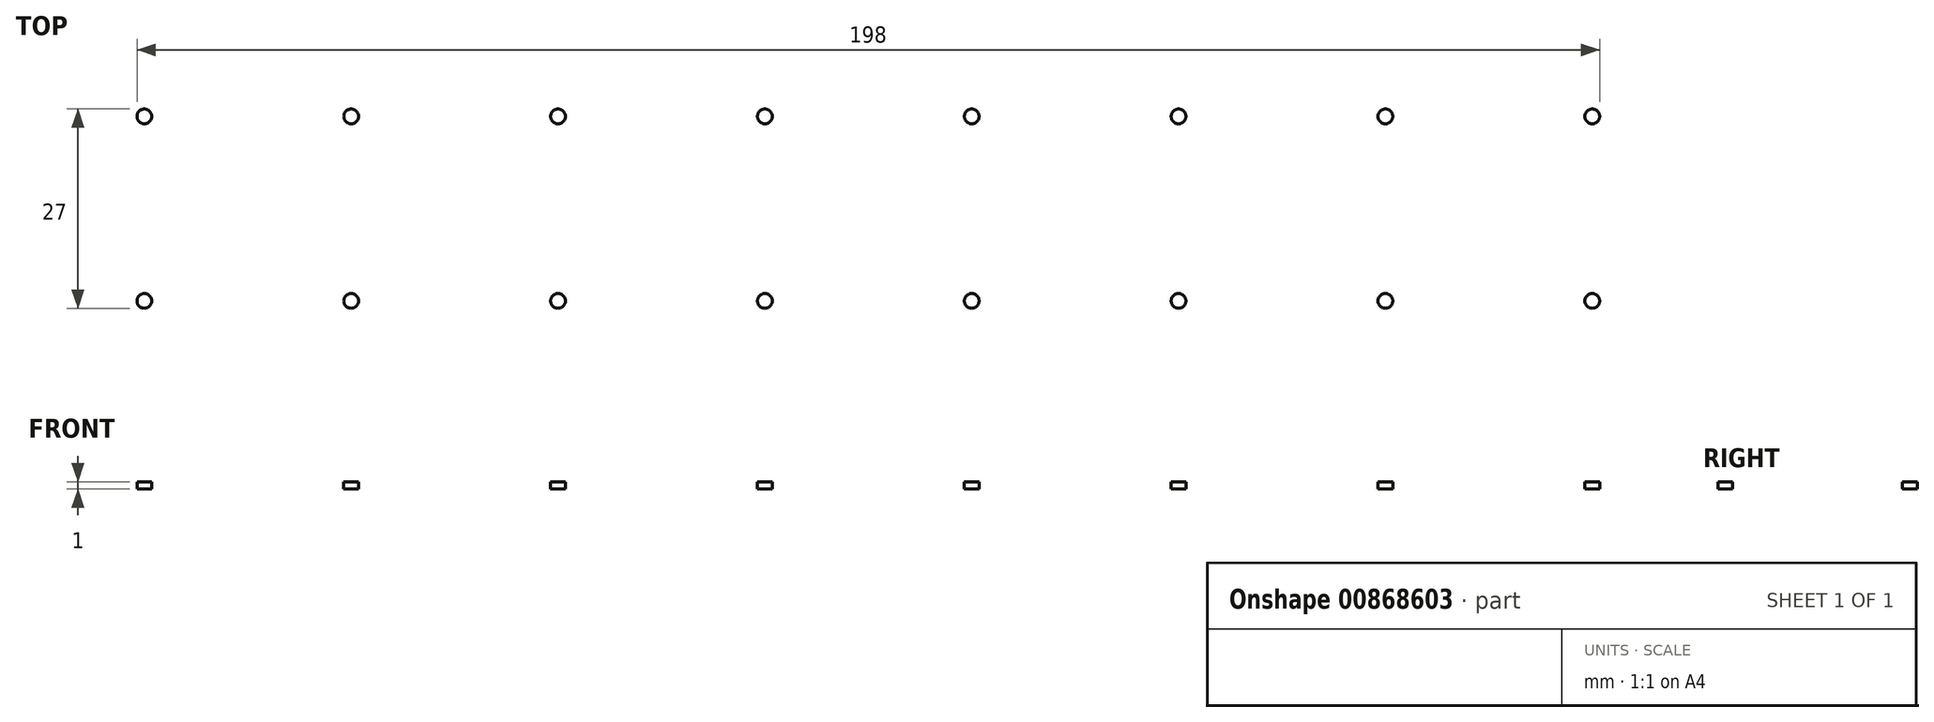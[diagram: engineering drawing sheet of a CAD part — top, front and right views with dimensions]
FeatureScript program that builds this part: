
annotation { "Feature Type Name" : "Feature", "Feature Type Description" : "" }
export const myFeature = defineFeature(function(context is Context, id is Id, definition is map)
    precondition{}
    {
        {
            var Q0;
            Q0=qCreatedBy(makeId("Top.planeOp"),FACE);
            var sketch = newSketch(context, id + "F0", { "sketchPlane" : qUnion([Q0])});
            skCircle(sketch, "E0", {"center": v(0, 0) * mm, "radius": 1 * mm});
            skLineSegment(sketch, "E1", {"start": v(-1, 0) * mm, "end": v(1, 0) * mm});
            skLineSegment(sketch, "E2", {"start": v(1, 0) * mm, "end": v(0, 0) * mm});
            skLineSegment(sketch, "E3", {"start": v(0, -1) * mm, "end": v(0, 1) * mm});
            skCircle(sketch, "E4.0.1.0", {"center": v(0, 25) * mm, "radius": 1 * mm});
            skLineSegment(sketch, "E4.0.1.1", {"start": v(-1, 25) * mm, "end": v(1, 25) * mm});
            skLineSegment(sketch, "E4.0.1.2", {"start": v(1, 25) * mm, "end": v(0, 25) * mm});
            skLineSegment(sketch, "E4.0.1.3", {"start": v(0, 24) * mm, "end": v(0, 26) * mm});
            skCircle(sketch, "E4.1.0.0", {"center": v(28, 0) * mm, "radius": 1 * mm});
            skLineSegment(sketch, "E4.1.0.1", {"start": v(27, 0) * mm, "end": v(29, 0) * mm});
            skLineSegment(sketch, "E4.1.0.2", {"start": v(29, 0) * mm, "end": v(28, 0) * mm});
            skLineSegment(sketch, "E4.1.0.3", {"start": v(28, -1) * mm, "end": v(28, 1) * mm});
            skCircle(sketch, "E4.1.1.0", {"center": v(28, 25) * mm, "radius": 1 * mm});
            skLineSegment(sketch, "E4.1.1.1", {"start": v(27, 25) * mm, "end": v(29, 25) * mm});
            skLineSegment(sketch, "E4.1.1.2", {"start": v(29, 25) * mm, "end": v(28, 25) * mm});
            skLineSegment(sketch, "E4.1.1.3", {"start": v(28, 24) * mm, "end": v(28, 26) * mm});
            skCircle(sketch, "E4.2.0.0", {"center": v(56, 0) * mm, "radius": 1 * mm});
            skLineSegment(sketch, "E4.2.0.1", {"start": v(55, 0) * mm, "end": v(57, 0) * mm});
            skLineSegment(sketch, "E4.2.0.2", {"start": v(57, 0) * mm, "end": v(56, 0) * mm});
            skLineSegment(sketch, "E4.2.0.3", {"start": v(56, -1) * mm, "end": v(56, 1) * mm});
            skCircle(sketch, "E4.2.1.0", {"center": v(56, 25) * mm, "radius": 1 * mm});
            skLineSegment(sketch, "E4.2.1.1", {"start": v(55, 25) * mm, "end": v(57, 25) * mm});
            skLineSegment(sketch, "E4.2.1.2", {"start": v(57, 25) * mm, "end": v(56, 25) * mm});
            skLineSegment(sketch, "E4.2.1.3", {"start": v(56, 24) * mm, "end": v(56, 26) * mm});
            skCircle(sketch, "E4.3.0.0", {"center": v(84, 0) * mm, "radius": 1 * mm});
            skLineSegment(sketch, "E4.3.0.1", {"start": v(83, 0) * mm, "end": v(85, 0) * mm});
            skLineSegment(sketch, "E4.3.0.2", {"start": v(85, 0) * mm, "end": v(84, 0) * mm});
            skLineSegment(sketch, "E4.3.0.3", {"start": v(84, -1) * mm, "end": v(84, 1) * mm});
            skCircle(sketch, "E4.3.1.0", {"center": v(84, 25) * mm, "radius": 1 * mm});
            skLineSegment(sketch, "E4.3.1.1", {"start": v(83, 25) * mm, "end": v(85, 25) * mm});
            skLineSegment(sketch, "E4.3.1.2", {"start": v(85, 25) * mm, "end": v(84, 25) * mm});
            skLineSegment(sketch, "E4.3.1.3", {"start": v(84, 24) * mm, "end": v(84, 26) * mm});
            skCircle(sketch, "E4.4.0.0", {"center": v(112, 0) * mm, "radius": 1 * mm});
            skLineSegment(sketch, "E4.4.0.1", {"start": v(111, 0) * mm, "end": v(113, 0) * mm});
            skLineSegment(sketch, "E4.4.0.2", {"start": v(113, 0) * mm, "end": v(112, 0) * mm});
            skLineSegment(sketch, "E4.4.0.3", {"start": v(112, -1) * mm, "end": v(112, 1) * mm});
            skCircle(sketch, "E4.4.1.0", {"center": v(112, 25) * mm, "radius": 1 * mm});
            skLineSegment(sketch, "E4.4.1.1", {"start": v(111, 25) * mm, "end": v(113, 25) * mm});
            skLineSegment(sketch, "E4.4.1.2", {"start": v(113, 25) * mm, "end": v(112, 25) * mm});
            skLineSegment(sketch, "E4.4.1.3", {"start": v(112, 24) * mm, "end": v(112, 26) * mm});
            skCircle(sketch, "E4.5.0.0", {"center": v(140, 0) * mm, "radius": 1 * mm});
            skLineSegment(sketch, "E4.5.0.1", {"start": v(139, 0) * mm, "end": v(141, 0) * mm});
            skLineSegment(sketch, "E4.5.0.2", {"start": v(141, 0) * mm, "end": v(140, 0) * mm});
            skLineSegment(sketch, "E4.5.0.3", {"start": v(140, -1) * mm, "end": v(140, 1) * mm});
            skCircle(sketch, "E4.5.1.0", {"center": v(140, 25) * mm, "radius": 1 * mm});
            skLineSegment(sketch, "E4.5.1.1", {"start": v(139, 25) * mm, "end": v(141, 25) * mm});
            skLineSegment(sketch, "E4.5.1.2", {"start": v(141, 25) * mm, "end": v(140, 25) * mm});
            skLineSegment(sketch, "E4.5.1.3", {"start": v(140, 24) * mm, "end": v(140, 26) * mm});
            skCircle(sketch, "E4.6.0.0", {"center": v(168, 0) * mm, "radius": 1 * mm});
            skLineSegment(sketch, "E4.6.0.1", {"start": v(167, 0) * mm, "end": v(169, 0) * mm});
            skLineSegment(sketch, "E4.6.0.2", {"start": v(169, 0) * mm, "end": v(168, 0) * mm});
            skLineSegment(sketch, "E4.6.0.3", {"start": v(168, -1) * mm, "end": v(168, 1) * mm});
            skCircle(sketch, "E4.6.1.0", {"center": v(168, 25) * mm, "radius": 1 * mm});
            skLineSegment(sketch, "E4.6.1.1", {"start": v(167, 25) * mm, "end": v(169, 25) * mm});
            skLineSegment(sketch, "E4.6.1.2", {"start": v(169, 25) * mm, "end": v(168, 25) * mm});
            skLineSegment(sketch, "E4.6.1.3", {"start": v(168, 24) * mm, "end": v(168, 26) * mm});
            skCircle(sketch, "E4.7.0.0", {"center": v(196, 0) * mm, "radius": 1 * mm});
            skLineSegment(sketch, "E4.7.0.1", {"start": v(195, 0) * mm, "end": v(197, 0) * mm});
            skLineSegment(sketch, "E4.7.0.2", {"start": v(197, 0) * mm, "end": v(196, 0) * mm});
            skLineSegment(sketch, "E4.7.0.3", {"start": v(196, -1) * mm, "end": v(196, 1) * mm});
            skCircle(sketch, "E4.7.1.0", {"center": v(196, 25) * mm, "radius": 1 * mm});
            skLineSegment(sketch, "E4.7.1.1", {"start": v(195, 25) * mm, "end": v(197, 25) * mm});
            skLineSegment(sketch, "E4.7.1.2", {"start": v(197, 25) * mm, "end": v(196, 25) * mm});
            skLineSegment(sketch, "E4.7.1.3", {"start": v(196, 24) * mm, "end": v(196, 26) * mm});
            skLineSegment(sketch, "E4.direction1", {"start": v(0, -1) * mm, "end": v(28, -1) * mm, "construction": true});
            skLineSegment(sketch, "E4.direction2", {"start": v(0, -1) * mm, "end": v(0, 24) * mm, "construction": true});
            skSolve(sketch);
        }
        {
            var Q0;
            {var subQ0=sQuery(id+"F0.wireOp",EDGE,"E4.7.1.2");Q0=makeQuery(id+"F0.imprint","IMPRINT",FACE,{"disambiguationData":[TD([[makeQuery(id+"F0.imprint","IMPRINT",EDGE,{"derivedFrom":subQ0}),1.0]])]});}
            var Q1;
            {var subQ0=sQuery(id+"F0.wireOp",EDGE,"E4.7.1.1");Q1=makeQuery(id+"F0.imprint","IMPRINT",FACE,{"disambiguationData":[TD([[makeQuery(id+"F0.imprint","IMPRINT",EDGE,{"derivedFrom":subQ0}),1.0]])]});}
            var Q2;
            {var subQ0=sQuery(id+"F0.wireOp",EDGE,"E4.7.1.1");Q2=makeQuery(id+"F0.imprint","IMPRINT",FACE,{"disambiguationData":[TD([[makeQuery(id+"F0.imprint","IMPRINT",EDGE,{"derivedFrom":subQ0}),-1.0]])]});}
            var Q3;
            {var subQ0=sQuery(id+"F0.wireOp",EDGE,"E4.7.1.2");Q3=makeQuery(id+"F0.imprint","IMPRINT",FACE,{"disambiguationData":[TD([[makeQuery(id+"F0.imprint","IMPRINT",EDGE,{"derivedFrom":subQ0}),-1.0]])]});}
            var Q4;
            {var subQ0=sQuery(id+"F0.wireOp",EDGE,"E4.6.1.2");Q4=makeQuery(id+"F0.imprint","IMPRINT",FACE,{"disambiguationData":[TD([[makeQuery(id+"F0.imprint","IMPRINT",EDGE,{"derivedFrom":subQ0}),-1.0]])]});}
            var Q5;
            {var subQ0=sQuery(id+"F0.wireOp",EDGE,"E4.6.1.1");Q5=makeQuery(id+"F0.imprint","IMPRINT",FACE,{"disambiguationData":[TD([[makeQuery(id+"F0.imprint","IMPRINT",EDGE,{"derivedFrom":subQ0}),1.0]])]});}
            var Q6;
            {var subQ0=sQuery(id+"F0.wireOp",EDGE,"E4.6.1.1");Q6=makeQuery(id+"F0.imprint","IMPRINT",FACE,{"disambiguationData":[TD([[makeQuery(id+"F0.imprint","IMPRINT",EDGE,{"derivedFrom":subQ0}),-1.0]])]});}
            var Q7;
            {var subQ0=sQuery(id+"F0.wireOp",EDGE,"E4.6.1.2");Q7=makeQuery(id+"F0.imprint","IMPRINT",FACE,{"disambiguationData":[TD([[makeQuery(id+"F0.imprint","IMPRINT",EDGE,{"derivedFrom":subQ0}),1.0]])]});}
            var Q8;
            {var subQ0=sQuery(id+"F0.wireOp",EDGE,"E4.7.0.2");Q8=makeQuery(id+"F0.imprint","IMPRINT",FACE,{"disambiguationData":[TD([[makeQuery(id+"F0.imprint","IMPRINT",EDGE,{"derivedFrom":subQ0}),-1.0]])]});}
            var Q9;
            {var subQ0=sQuery(id+"F0.wireOp",EDGE,"E4.7.0.1");Q9=makeQuery(id+"F0.imprint","IMPRINT",FACE,{"disambiguationData":[TD([[makeQuery(id+"F0.imprint","IMPRINT",EDGE,{"derivedFrom":subQ0}),1.0]])]});}
            var Q10;
            {var subQ0=sQuery(id+"F0.wireOp",EDGE,"E4.7.0.1");Q10=makeQuery(id+"F0.imprint","IMPRINT",FACE,{"disambiguationData":[TD([[makeQuery(id+"F0.imprint","IMPRINT",EDGE,{"derivedFrom":subQ0}),-1.0]])]});}
            var Q11;
            {var subQ0=sQuery(id+"F0.wireOp",EDGE,"E4.7.0.2");Q11=makeQuery(id+"F0.imprint","IMPRINT",FACE,{"disambiguationData":[TD([[makeQuery(id+"F0.imprint","IMPRINT",EDGE,{"derivedFrom":subQ0}),1.0]])]});}
            var Q12;
            {var subQ0=sQuery(id+"F0.wireOp",EDGE,"E4.0.1.2");Q12=makeQuery(id+"F0.imprint","IMPRINT",FACE,{"disambiguationData":[TD([[makeQuery(id+"F0.imprint","IMPRINT",EDGE,{"derivedFrom":subQ0}),-1.0]])]});}
            var Q13;
            {var subQ0=sQuery(id+"F0.wireOp",EDGE,"E4.0.1.1");Q13=makeQuery(id+"F0.imprint","IMPRINT",FACE,{"disambiguationData":[TD([[makeQuery(id+"F0.imprint","IMPRINT",EDGE,{"derivedFrom":subQ0}),1.0]])]});}
            var Q14;
            {var subQ0=sQuery(id+"F0.wireOp",EDGE,"E4.0.1.1");Q14=makeQuery(id+"F0.imprint","IMPRINT",FACE,{"disambiguationData":[TD([[makeQuery(id+"F0.imprint","IMPRINT",EDGE,{"derivedFrom":subQ0}),-1.0]])]});}
            var Q15;
            {var subQ0=sQuery(id+"F0.wireOp",EDGE,"E4.0.1.2");Q15=makeQuery(id+"F0.imprint","IMPRINT",FACE,{"disambiguationData":[TD([[makeQuery(id+"F0.imprint","IMPRINT",EDGE,{"derivedFrom":subQ0}),1.0]])]});}
            var Q16;
            {var subQ0=sQuery(id+"F0.wireOp",EDGE,"E4.1.0.2");Q16=makeQuery(id+"F0.imprint","IMPRINT",FACE,{"disambiguationData":[TD([[makeQuery(id+"F0.imprint","IMPRINT",EDGE,{"derivedFrom":subQ0}),-1.0]])]});}
            var Q17;
            {var subQ0=sQuery(id+"F0.wireOp",EDGE,"E4.1.0.1");Q17=makeQuery(id+"F0.imprint","IMPRINT",FACE,{"disambiguationData":[TD([[makeQuery(id+"F0.imprint","IMPRINT",EDGE,{"derivedFrom":subQ0}),1.0]])]});}
            var Q18;
            {var subQ0=sQuery(id+"F0.wireOp",EDGE,"E4.1.0.1");Q18=makeQuery(id+"F0.imprint","IMPRINT",FACE,{"disambiguationData":[TD([[makeQuery(id+"F0.imprint","IMPRINT",EDGE,{"derivedFrom":subQ0}),-1.0]])]});}
            var Q19;
            {var subQ0=sQuery(id+"F0.wireOp",EDGE,"E4.1.0.2");Q19=makeQuery(id+"F0.imprint","IMPRINT",FACE,{"disambiguationData":[TD([[makeQuery(id+"F0.imprint","IMPRINT",EDGE,{"derivedFrom":subQ0}),1.0]])]});}
            var Q20;
            {var subQ0=sQuery(id+"F0.wireOp",EDGE,"E4.1.1.2");Q20=makeQuery(id+"F0.imprint","IMPRINT",FACE,{"disambiguationData":[TD([[makeQuery(id+"F0.imprint","IMPRINT",EDGE,{"derivedFrom":subQ0}),1.0]])]});}
            var Q21;
            {var subQ0=sQuery(id+"F0.wireOp",EDGE,"E4.1.1.1");Q21=makeQuery(id+"F0.imprint","IMPRINT",FACE,{"disambiguationData":[TD([[makeQuery(id+"F0.imprint","IMPRINT",EDGE,{"derivedFrom":subQ0}),1.0]])]});}
            var Q22;
            {var subQ0=sQuery(id+"F0.wireOp",EDGE,"E4.1.1.1");Q22=makeQuery(id+"F0.imprint","IMPRINT",FACE,{"disambiguationData":[TD([[makeQuery(id+"F0.imprint","IMPRINT",EDGE,{"derivedFrom":subQ0}),-1.0]])]});}
            var Q23;
            {var subQ0=sQuery(id+"F0.wireOp",EDGE,"E4.2.0.2");Q23=makeQuery(id+"F0.imprint","IMPRINT",FACE,{"disambiguationData":[TD([[makeQuery(id+"F0.imprint","IMPRINT",EDGE,{"derivedFrom":subQ0}),-1.0]])]});}
            var Q24;
            {var subQ0=sQuery(id+"F0.wireOp",EDGE,"E4.2.0.1");Q24=makeQuery(id+"F0.imprint","IMPRINT",FACE,{"disambiguationData":[TD([[makeQuery(id+"F0.imprint","IMPRINT",EDGE,{"derivedFrom":subQ0}),1.0]])]});}
            var Q25;
            {var subQ0=sQuery(id+"F0.wireOp",EDGE,"E4.2.0.1");Q25=makeQuery(id+"F0.imprint","IMPRINT",FACE,{"disambiguationData":[TD([[makeQuery(id+"F0.imprint","IMPRINT",EDGE,{"derivedFrom":subQ0}),-1.0]])]});}
            var Q26;
            {var subQ0=sQuery(id+"F0.wireOp",EDGE,"E4.2.0.2");Q26=makeQuery(id+"F0.imprint","IMPRINT",FACE,{"disambiguationData":[TD([[makeQuery(id+"F0.imprint","IMPRINT",EDGE,{"derivedFrom":subQ0}),1.0]])]});}
            var Q27;
            {var subQ0=sQuery(id+"F0.wireOp",EDGE,"E4.2.1.2");Q27=makeQuery(id+"F0.imprint","IMPRINT",FACE,{"disambiguationData":[TD([[makeQuery(id+"F0.imprint","IMPRINT",EDGE,{"derivedFrom":subQ0}),-1.0]])]});}
            var Q28;
            {var subQ0=sQuery(id+"F0.wireOp",EDGE,"E4.2.1.1");Q28=makeQuery(id+"F0.imprint","IMPRINT",FACE,{"disambiguationData":[TD([[makeQuery(id+"F0.imprint","IMPRINT",EDGE,{"derivedFrom":subQ0}),1.0]])]});}
            var Q29;
            {var subQ0=sQuery(id+"F0.wireOp",EDGE,"E4.2.1.1");Q29=makeQuery(id+"F0.imprint","IMPRINT",FACE,{"disambiguationData":[TD([[makeQuery(id+"F0.imprint","IMPRINT",EDGE,{"derivedFrom":subQ0}),-1.0]])]});}
            var Q30;
            {var subQ0=sQuery(id+"F0.wireOp",EDGE,"E4.2.1.2");Q30=makeQuery(id+"F0.imprint","IMPRINT",FACE,{"disambiguationData":[TD([[makeQuery(id+"F0.imprint","IMPRINT",EDGE,{"derivedFrom":subQ0}),1.0]])]});}
            var Q31;
            {var subQ0=sQuery(id+"F0.wireOp",EDGE,"E4.3.0.2");Q31=makeQuery(id+"F0.imprint","IMPRINT",FACE,{"disambiguationData":[TD([[makeQuery(id+"F0.imprint","IMPRINT",EDGE,{"derivedFrom":subQ0}),-1.0]])]});}
            var Q32;
            {var subQ0=sQuery(id+"F0.wireOp",EDGE,"E4.3.0.1");Q32=makeQuery(id+"F0.imprint","IMPRINT",FACE,{"disambiguationData":[TD([[makeQuery(id+"F0.imprint","IMPRINT",EDGE,{"derivedFrom":subQ0}),1.0]])]});}
            var Q33;
            {var subQ0=sQuery(id+"F0.wireOp",EDGE,"E4.3.0.1");Q33=makeQuery(id+"F0.imprint","IMPRINT",FACE,{"disambiguationData":[TD([[makeQuery(id+"F0.imprint","IMPRINT",EDGE,{"derivedFrom":subQ0}),-1.0]])]});}
            var Q34;
            {var subQ0=sQuery(id+"F0.wireOp",EDGE,"E4.3.0.2");Q34=makeQuery(id+"F0.imprint","IMPRINT",FACE,{"disambiguationData":[TD([[makeQuery(id+"F0.imprint","IMPRINT",EDGE,{"derivedFrom":subQ0}),1.0]])]});}
            var Q35;
            {var subQ0=sQuery(id+"F0.wireOp",EDGE,"E4.3.1.2");Q35=makeQuery(id+"F0.imprint","IMPRINT",FACE,{"disambiguationData":[TD([[makeQuery(id+"F0.imprint","IMPRINT",EDGE,{"derivedFrom":subQ0}),1.0]])]});}
            var Q36;
            {var subQ0=sQuery(id+"F0.wireOp",EDGE,"E4.3.1.1");Q36=makeQuery(id+"F0.imprint","IMPRINT",FACE,{"disambiguationData":[TD([[makeQuery(id+"F0.imprint","IMPRINT",EDGE,{"derivedFrom":subQ0}),-1.0]])]});}
            var Q37;
            {var subQ0=sQuery(id+"F0.wireOp",EDGE,"E4.3.1.2");Q37=makeQuery(id+"F0.imprint","IMPRINT",FACE,{"disambiguationData":[TD([[makeQuery(id+"F0.imprint","IMPRINT",EDGE,{"derivedFrom":subQ0}),-1.0]])]});}
            var Q38;
            {var subQ0=sQuery(id+"F0.wireOp",EDGE,"E4.4.0.2");Q38=makeQuery(id+"F0.imprint","IMPRINT",FACE,{"disambiguationData":[TD([[makeQuery(id+"F0.imprint","IMPRINT",EDGE,{"derivedFrom":subQ0}),-1.0]])]});}
            var Q39;
            {var subQ0=sQuery(id+"F0.wireOp",EDGE,"E4.4.0.1");Q39=makeQuery(id+"F0.imprint","IMPRINT",FACE,{"disambiguationData":[TD([[makeQuery(id+"F0.imprint","IMPRINT",EDGE,{"derivedFrom":subQ0}),1.0]])]});}
            var Q40;
            {var subQ0=sQuery(id+"F0.wireOp",EDGE,"E4.4.0.1");Q40=makeQuery(id+"F0.imprint","IMPRINT",FACE,{"disambiguationData":[TD([[makeQuery(id+"F0.imprint","IMPRINT",EDGE,{"derivedFrom":subQ0}),-1.0]])]});}
            var Q41;
            {var subQ0=sQuery(id+"F0.wireOp",EDGE,"E4.4.0.2");Q41=makeQuery(id+"F0.imprint","IMPRINT",FACE,{"disambiguationData":[TD([[makeQuery(id+"F0.imprint","IMPRINT",EDGE,{"derivedFrom":subQ0}),1.0]])]});}
            var Q42;
            {var subQ0=sQuery(id+"F0.wireOp",EDGE,"E4.4.1.2");Q42=makeQuery(id+"F0.imprint","IMPRINT",FACE,{"disambiguationData":[TD([[makeQuery(id+"F0.imprint","IMPRINT",EDGE,{"derivedFrom":subQ0}),-1.0]])]});}
            var Q43;
            {var subQ0=sQuery(id+"F0.wireOp",EDGE,"E4.4.1.1");Q43=makeQuery(id+"F0.imprint","IMPRINT",FACE,{"disambiguationData":[TD([[makeQuery(id+"F0.imprint","IMPRINT",EDGE,{"derivedFrom":subQ0}),1.0]])]});}
            var Q44;
            {var subQ0=sQuery(id+"F0.wireOp",EDGE,"E4.4.1.1");Q44=makeQuery(id+"F0.imprint","IMPRINT",FACE,{"disambiguationData":[TD([[makeQuery(id+"F0.imprint","IMPRINT",EDGE,{"derivedFrom":subQ0}),-1.0]])]});}
            var Q45;
            {var subQ0=sQuery(id+"F0.wireOp",EDGE,"E4.4.1.2");Q45=makeQuery(id+"F0.imprint","IMPRINT",FACE,{"disambiguationData":[TD([[makeQuery(id+"F0.imprint","IMPRINT",EDGE,{"derivedFrom":subQ0}),1.0]])]});}
            var Q46;
            {var subQ0=sQuery(id+"F0.wireOp",EDGE,"E4.5.0.2");Q46=makeQuery(id+"F0.imprint","IMPRINT",FACE,{"disambiguationData":[TD([[makeQuery(id+"F0.imprint","IMPRINT",EDGE,{"derivedFrom":subQ0}),-1.0]])]});}
            var Q47;
            {var subQ0=sQuery(id+"F0.wireOp",EDGE,"E4.5.0.1");Q47=makeQuery(id+"F0.imprint","IMPRINT",FACE,{"disambiguationData":[TD([[makeQuery(id+"F0.imprint","IMPRINT",EDGE,{"derivedFrom":subQ0}),1.0]])]});}
            var Q48;
            {var subQ0=sQuery(id+"F0.wireOp",EDGE,"E4.5.0.1");Q48=makeQuery(id+"F0.imprint","IMPRINT",FACE,{"disambiguationData":[TD([[makeQuery(id+"F0.imprint","IMPRINT",EDGE,{"derivedFrom":subQ0}),-1.0]])]});}
            var Q49;
            {var subQ0=sQuery(id+"F0.wireOp",EDGE,"E4.5.0.2");Q49=makeQuery(id+"F0.imprint","IMPRINT",FACE,{"disambiguationData":[TD([[makeQuery(id+"F0.imprint","IMPRINT",EDGE,{"derivedFrom":subQ0}),1.0]])]});}
            var Q50;
            {var subQ0=sQuery(id+"F0.wireOp",EDGE,"E4.5.1.2");Q50=makeQuery(id+"F0.imprint","IMPRINT",FACE,{"disambiguationData":[TD([[makeQuery(id+"F0.imprint","IMPRINT",EDGE,{"derivedFrom":subQ0}),1.0]])]});}
            var Q51;
            {var subQ0=sQuery(id+"F0.wireOp",EDGE,"E4.5.1.1");Q51=makeQuery(id+"F0.imprint","IMPRINT",FACE,{"disambiguationData":[TD([[makeQuery(id+"F0.imprint","IMPRINT",EDGE,{"derivedFrom":subQ0}),1.0]])]});}
            var Q52;
            {var subQ0=sQuery(id+"F0.wireOp",EDGE,"E4.5.1.1");Q52=makeQuery(id+"F0.imprint","IMPRINT",FACE,{"disambiguationData":[TD([[makeQuery(id+"F0.imprint","IMPRINT",EDGE,{"derivedFrom":subQ0}),-1.0]])]});}
            var Q53;
            {var subQ0=sQuery(id+"F0.wireOp",EDGE,"E4.5.1.2");Q53=makeQuery(id+"F0.imprint","IMPRINT",FACE,{"disambiguationData":[TD([[makeQuery(id+"F0.imprint","IMPRINT",EDGE,{"derivedFrom":subQ0}),-1.0]])]});}
            var Q54;
            {var subQ0=sQuery(id+"F0.wireOp",EDGE,"E4.6.0.2");Q54=makeQuery(id+"F0.imprint","IMPRINT",FACE,{"disambiguationData":[TD([[makeQuery(id+"F0.imprint","IMPRINT",EDGE,{"derivedFrom":subQ0}),-1.0]])]});}
            var Q55;
            {var subQ0=sQuery(id+"F0.wireOp",EDGE,"E4.6.0.1");Q55=makeQuery(id+"F0.imprint","IMPRINT",FACE,{"disambiguationData":[TD([[makeQuery(id+"F0.imprint","IMPRINT",EDGE,{"derivedFrom":subQ0}),1.0]])]});}
            var Q56;
            {var subQ0=sQuery(id+"F0.wireOp",EDGE,"E4.6.0.1");Q56=makeQuery(id+"F0.imprint","IMPRINT",FACE,{"disambiguationData":[TD([[makeQuery(id+"F0.imprint","IMPRINT",EDGE,{"derivedFrom":subQ0}),-1.0]])]});}
            var Q57;
            {var subQ0=sQuery(id+"F0.wireOp",EDGE,"E4.6.0.2");Q57=makeQuery(id+"F0.imprint","IMPRINT",FACE,{"disambiguationData":[TD([[makeQuery(id+"F0.imprint","IMPRINT",EDGE,{"derivedFrom":subQ0}),1.0]])]});}
            var Q58;
            {var subQ0=sQuery(id+"F0.wireOp",EDGE,"E2");Q58=makeQuery(id+"F0.imprint","IMPRINT",FACE,{"disambiguationData":[TD([[makeQuery(id+"F0.imprint","IMPRINT",EDGE,{"derivedFrom":subQ0}),-1.0]])]});}
            var Q59;
            {var subQ0=sQuery(id+"F0.wireOp",EDGE,"E1");Q59=makeQuery(id+"F0.imprint","IMPRINT",FACE,{"disambiguationData":[TD([[makeQuery(id+"F0.imprint","IMPRINT",EDGE,{"derivedFrom":subQ0}),1.0]])]});}
            var Q60;
            {var subQ0=sQuery(id+"F0.wireOp",EDGE,"E1");Q60=makeQuery(id+"F0.imprint","IMPRINT",FACE,{"disambiguationData":[TD([[makeQuery(id+"F0.imprint","IMPRINT",EDGE,{"derivedFrom":subQ0}),-1.0]])]});}
            var Q61;
            {var subQ0=sQuery(id+"F0.wireOp",EDGE,"E2");Q61=makeQuery(id+"F0.imprint","IMPRINT",FACE,{"disambiguationData":[TD([[makeQuery(id+"F0.imprint","IMPRINT",EDGE,{"derivedFrom":subQ0}),1.0]])]});}
            var Q62;
            {var subQ0=sQuery(id+"F0.wireOp",EDGE,"E4.1.1.2");Q62=makeQuery(id+"F0.imprint","IMPRINT",FACE,{"disambiguationData":[TD([[makeQuery(id+"F0.imprint","IMPRINT",EDGE,{"derivedFrom":subQ0}),-1.0]])]});}
            var Q63;
            {var subQ0=sQuery(id+"F0.wireOp",EDGE,"E4.3.1.1");Q63=makeQuery(id+"F0.imprint","IMPRINT",FACE,{"disambiguationData":[TD([[makeQuery(id+"F0.imprint","IMPRINT",EDGE,{"derivedFrom":subQ0}),1.0]])]});}
            extrude(context, id + "F1", {"entities" : qUnion([Q0, Q1, Q2, Q3, Q4, Q5, Q6, Q7, Q8, Q9, Q10, Q11, Q12, Q13, Q14, Q15, Q16, Q17, Q18, Q19, Q20, Q21, Q22, Q23, Q24, Q25, Q26, Q27, Q28, Q29, Q30, Q31, Q32, Q33, Q34, Q35, Q36, Q37, Q38, Q39, Q40, Q41, Q42, Q43, Q44, Q45, Q46, Q47, Q48, Q49, Q50, Q51, Q52, Q53, Q54, Q55, Q56, Q57, Q58, Q59, Q60, Q61, Q62, Q63]), "depth" : 1 * mm, "offsetDistance" : 25 * mm});
        }
    });
